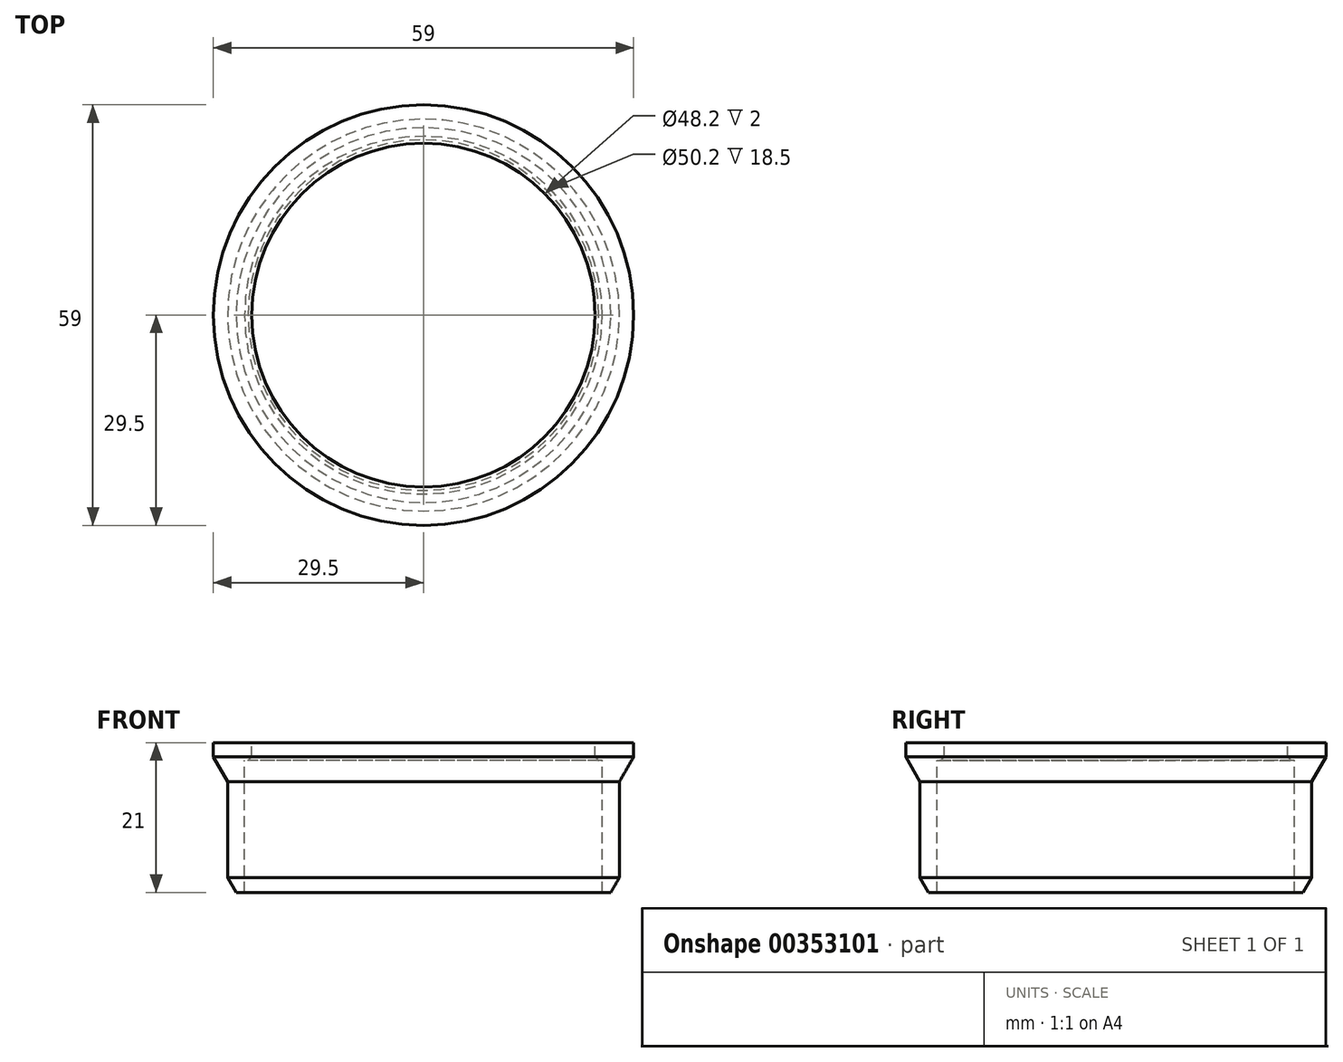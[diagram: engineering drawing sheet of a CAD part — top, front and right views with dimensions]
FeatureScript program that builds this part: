
annotation { "Feature Type Name" : "Feature", "Feature Type Description" : "" }
export const myFeature = defineFeature(function(context is Context, id is Id, definition is map)
    precondition{}
    {
        {
            var Q0;
            Q0=qCreatedBy(makeId("Front.planeOp"),FACE);
            var sketch = newSketch(context, id + "F0", { "sketchPlane" : qUnion([Q0])});
            skLineSegment(sketch, "E0", {"start": v(24.1, -14.37) * mm, "end": v(24.1, -16.37) * mm});
            skLineSegment(sketch, "E1", {"start": v(25.1, -16.87) * mm, "end": v(24.6, -16.87) * mm});
            skLineSegment(sketch, "E2", {"start": v(25.1, -16.87) * mm, "end": v(25.1, -35.37) * mm});
            skLineSegment(sketch, "E3", {"start": v(25.1, -35.37) * mm, "end": v(26.3, -35.37) * mm});
            skLineSegment(sketch, "E4", {"start": v(26.3, -35.37) * mm, "end": v(27.5, -33.3) * mm});
            skLineSegment(sketch, "E5", {"start": v(29.5, -16.37) * mm, "end": v(29.5, -14.37) * mm});
            skLineSegment(sketch, "E6", {"start": v(29.5, -14.37) * mm, "end": v(24.1, -14.37) * mm});
            skLineSegment(sketch, "E7", {"start": v(0, 24.42) * mm, "end": v(0, -13.18) * mm, "construction": true});
            skLineSegment(sketch, "E8", {"start": v(24.6, -16.87) * mm, "end": v(24.1, -16.37) * mm});
            skPoint(sketch, "E9.orphan", {"position": v(24.1, -16.87) * mm});
            skLineSegment(sketch, "E10", {"start": v(27.5, -33.3) * mm, "end": v(27.5, -19.83) * mm});
            skLineSegment(sketch, "E11", {"start": v(27.5, -19.83) * mm, "end": v(29.5, -16.37) * mm});
            skSolve(sketch);
        }
        {
            var Q0;
            Q0=makeQuery(id+"F0.imprint","IMPRINT",FACE,{"disambiguationData":[TD([[makeQuery(id+"F0.imprint","IMPRINT",EDGE,{"derivedFrom":sQuery(id+"F0.wireOp",EDGE,"E0")}),1.0]])]});
            var Q1;
            Q1=sQuery(id+"F0.wireOp",EDGE,"E7");
            revolve(context, id + "F1", {"entities" : qUnion([Q0]), "axis" : qUnion([Q1]), "revolveType" : RevolveType.FULL});
        }
    });
